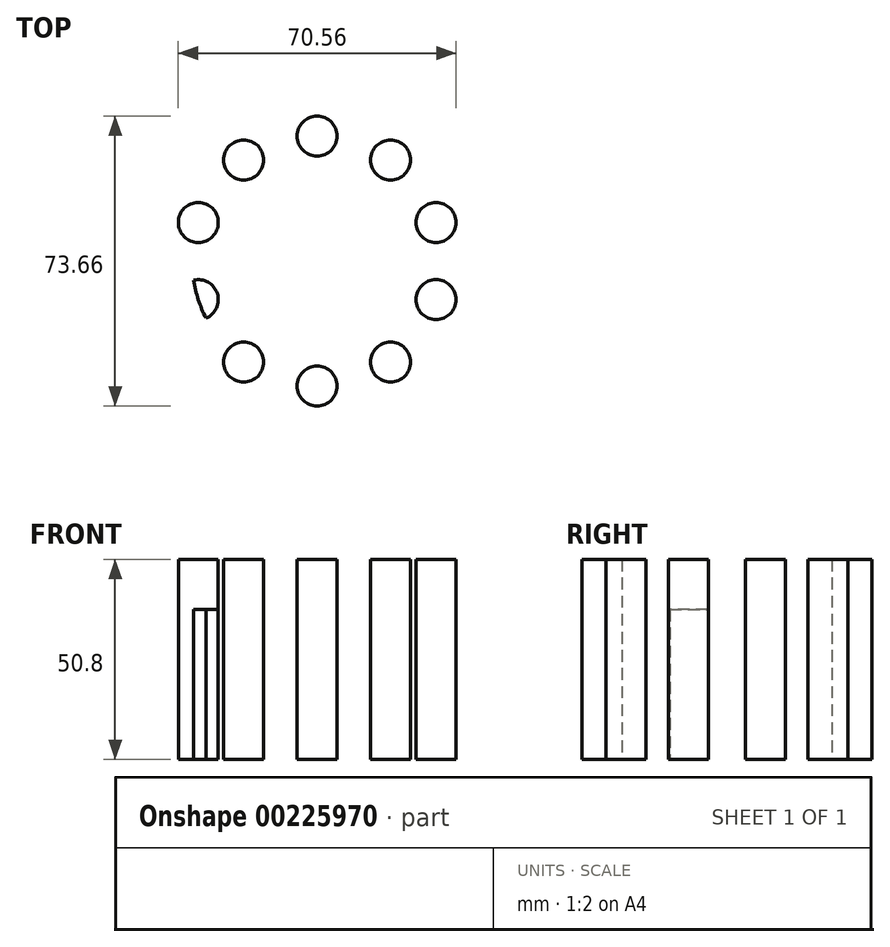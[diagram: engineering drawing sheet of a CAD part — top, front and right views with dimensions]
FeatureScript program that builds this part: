
annotation { "Feature Type Name" : "Feature", "Feature Type Description" : "" }
export const myFeature = defineFeature(function(context is Context, id is Id, definition is map)
    precondition{}
    {
        {
            var Q0;
            Q0=qCreatedBy(makeId("Top.planeOp"),FACE);
            var sketch = newSketch(context, id + "F0", { "sketchPlane" : qUnion([Q0])});
            skCircle(sketch, "E0", {"center": v(0, 0) * mm, "radius": 31.75 * mm});
            skSolve(sketch);
        }
        {
            var Q0;
            Q0=qSketchRegion(id+"F0",true);
            extrude(context, id + "F1", {"entities" : qUnion([Q0]), "depth" : 38.1 * mm});
        }
        {
            var Q0;
            Q0=qCreatedBy(makeId("Top.planeOp"),FACE);
            var sketch = newSketch(context, id + "F2", { "sketchPlane" : qUnion([Q0])});
            skCircle(sketch, "E1", {"center": v(0, 31.75) * mm, "radius": 5.08 * mm});
            skCircle(sketch, "E2.1.0", {"center": v(-18.66, 25.69) * mm, "radius": 5.08 * mm});
            skCircle(sketch, "E2.2.0", {"center": v(-30.2, 9.81) * mm, "radius": 5.08 * mm});
            skCircle(sketch, "E2.3.0", {"center": v(-30.2, -9.81) * mm, "radius": 5.08 * mm});
            skCircle(sketch, "E2.4.0", {"center": v(-18.66, -25.69) * mm, "radius": 5.08 * mm});
            skCircle(sketch, "E2.5.0", {"center": v(0, -31.75) * mm, "radius": 5.08 * mm});
            skCircle(sketch, "E2.6.0", {"center": v(18.66, -25.69) * mm, "radius": 5.08 * mm});
            skCircle(sketch, "E2.7.0", {"center": v(30.2, -9.81) * mm, "radius": 5.08 * mm});
            skCircle(sketch, "E2.8.0", {"center": v(30.2, 9.81) * mm, "radius": 5.08 * mm});
            skCircle(sketch, "E2.9.0", {"center": v(18.66, 25.69) * mm, "radius": 5.08 * mm});
            skPoint(sketch, "E2.center", {"position": v(0, 0) * mm});
            skSolve(sketch);
        }
        {
            var Q0;
            Q0=qSketchRegion(id+"F2",true);
            extrude(context, id + "F3", {"entities" : qUnion([Q0]), "depth" : 50.8 * mm});
        }
        {
            var Q0;
            Q0=makeQuery(id+"F3.opExtrude","SWEPT_BODY",BODY,{"disambiguationData":[OSD([sQuery(id+"F2.wireOp",EDGE,"E2.3.0")])]});
            var Q1;
            Q1=makeQuery(id+"F1.opExtrude","SWEPT_BODY",BODY,{"disambiguationData":[OSD([sQuery(id+"F0.wireOp",EDGE,"E0")])]});
            booleanBodies(context, id + "F4", {"operationType" : BooleanOperationType.INTERSECTION, "tools" : qUnion([Q0, Q1])});
        }
    });
